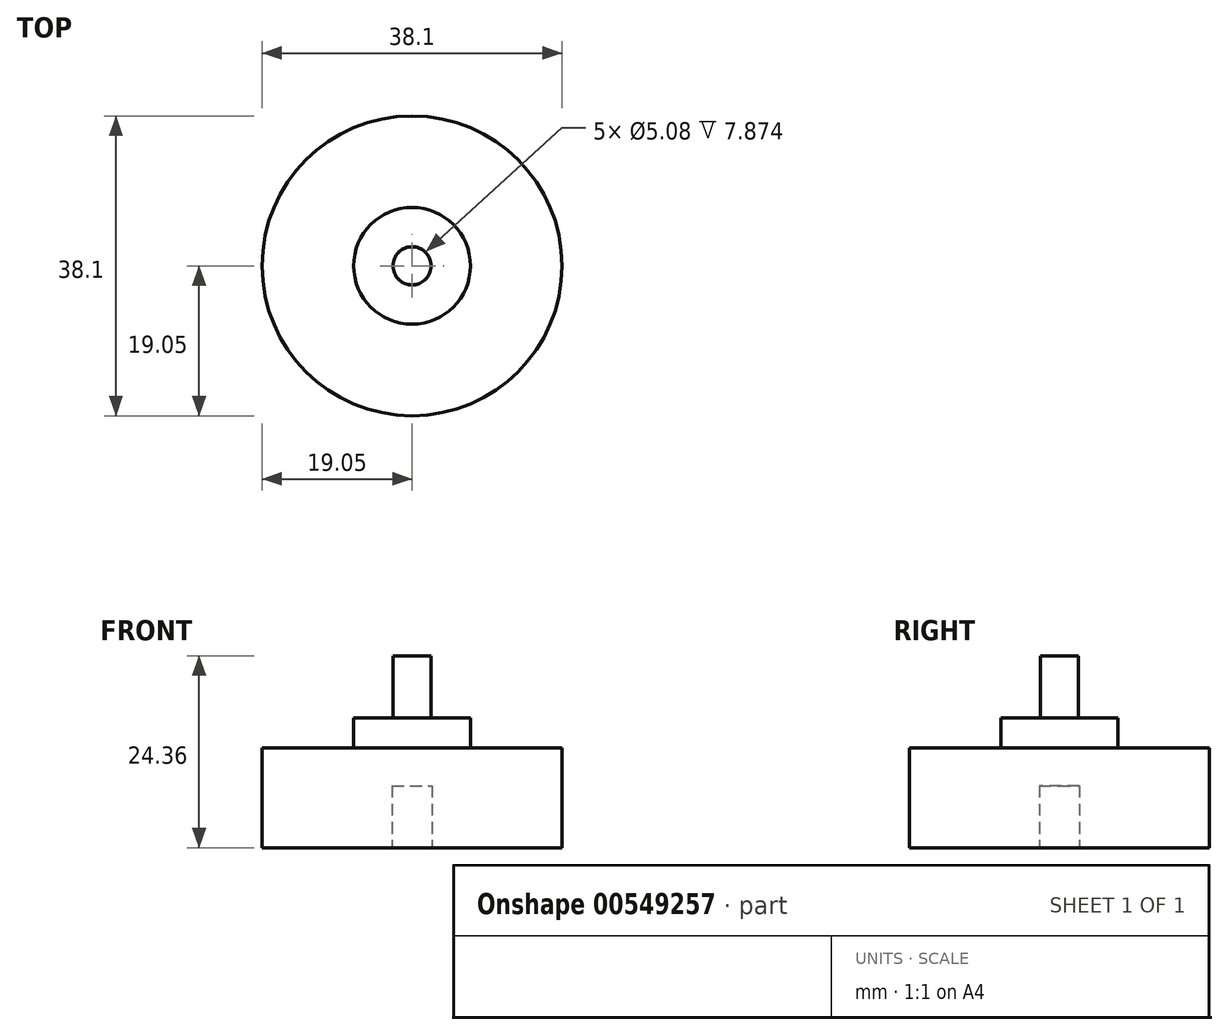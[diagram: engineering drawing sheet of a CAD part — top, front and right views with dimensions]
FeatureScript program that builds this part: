
annotation { "Feature Type Name" : "Feature", "Feature Type Description" : "" }
export const myFeature = defineFeature(function(context is Context, id is Id, definition is map)
    precondition{}
    {
        {
            var Q0;
            Q0=qCreatedBy(makeId("Front.planeOp"),FACE);
            var sketch = newSketch(context, id + "F0", { "sketchPlane" : qUnion([Q0])});
            skLineSegment(sketch, "E0", {"start": v(19.05, 0) * mm, "end": v(19.05, 12.7) * mm});
            skLineSegment(sketch, "E1", {"start": v(19.05, 12.7) * mm, "end": v(7.42, 12.7) * mm});
            skLineSegment(sketch, "E2", {"start": v(2.41, 16.51) * mm, "end": v(7.42, 16.51) * mm});
            skLineSegment(sketch, "E3", {"start": v(7.42, 16.51) * mm, "end": v(7.42, 12.7) * mm});
            skLineSegment(sketch, "E4", {"start": v(0, 24.36) * mm, "end": v(2.41, 24.36) * mm});
            skLineSegment(sketch, "E5", {"start": v(2.41, 24.36) * mm, "end": v(2.41, 16.51) * mm});
            skPoint(sketch, "E6.start.orphan", {"position": v(0, 12.7) * mm});
            skPoint(sketch, "E7.start.orphan", {"position": v(0, 16.51) * mm});
            skLineSegment(sketch, "E8", {"start": v(2.54, 0) * mm, "end": v(2.54, 7.87) * mm});
            skLineSegment(sketch, "E9", {"start": v(2.54, 7.87) * mm, "end": v(0, 7.87) * mm});
            skLineSegment(sketch, "E10", {"start": v(0, 7.87) * mm, "end": v(0, 24.36) * mm});
            skLineSegment(sketch, "E11", {"start": v(19.05, 0) * mm, "end": v(2.54, 0) * mm});
            skSolve(sketch);
        }
        {
            var Q0;
            Q0 = qSketchRegion(id + "F0", true);
            var Q1;
            Q1=sQuery(id+"F0.wireOp",EDGE,"E10");
            revolve(context, id + "F1", {"entities" : qUnion([Q0]), "axis" : qUnion([Q1]), "revolveType" : RevolveType.FULL});
        }
    });
